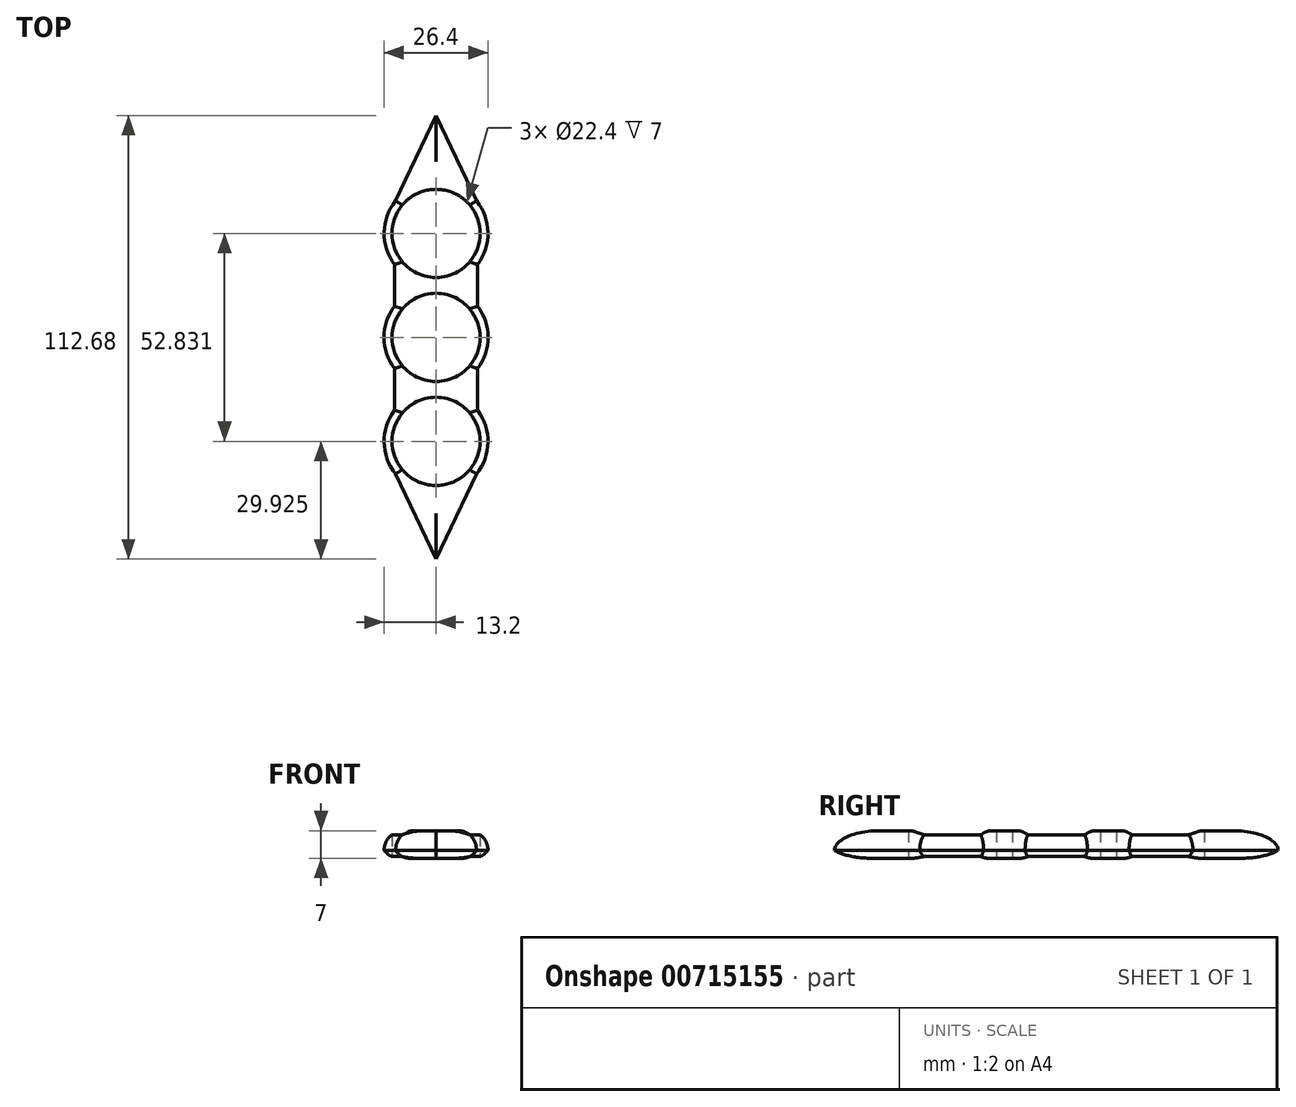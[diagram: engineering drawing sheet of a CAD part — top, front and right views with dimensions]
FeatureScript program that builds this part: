
annotation { "Feature Type Name" : "Feature", "Feature Type Description" : "" }
export const myFeature = defineFeature(function(context is Context, id is Id, definition is map)
    precondition{}
    {
        {
            var Q0;
            Q0=qCreatedBy(makeId("Top.planeOp"),FACE);
            var sketch = newSketch(context, id + "F0", { "sketchPlane" : qUnion([Q0])});
            skCircle(sketch, "E0", {"center": v(0, 0) * mm, "radius": 11.2 * mm});
            skCircle(sketch, "E1", {"center": v(0, 0) * mm, "radius": 13.2 * mm});
            skCircle(sketch, "E2", {"center": v(0, 26.42) * mm, "radius": 11.2 * mm});
            skArc(sketch, "E3", {"start": v(10.55, 18.48) * mm, "mid": v(0, 39.62) * mm, "end": v(-10.55, 18.48) * mm});
            skArc(sketch, "E4.1.0", {"start": v(-10.55, -18.48) * mm, "mid": v(0, -39.62) * mm, "end": v(10.55, -18.48) * mm});
            skCircle(sketch, "E4.1.1", {"center": v(0, -26.42) * mm, "radius": 11.2 * mm});
            skLineSegment(sketch, "E5", {"start": v(-10.55, 18.48) * mm, "end": v(-10.55, 7.93) * mm});
            skLineSegment(sketch, "E6", {"start": v(10.55, 18.48) * mm, "end": v(10.55, 7.93) * mm});
            skLineSegment(sketch, "E7.1.0", {"start": v(-10.55, -18.48) * mm, "end": v(-10.55, -7.93) * mm});
            skLineSegment(sketch, "E7.1.1", {"start": v(10.55, -18.48) * mm, "end": v(10.55, -7.93) * mm});
            skLineSegment(sketch, "E8", {"start": v(10.28, 34.7) * mm, "end": v(0, 56.34) * mm});
            skPoint(sketch, "E8.endSnap0", {"position": v(0, 39.62) * mm});
            skLineSegment(sketch, "E9", {"start": v(0, 56.34) * mm, "end": v(-10.28, 34.7) * mm});
            skLineSegment(sketch, "E10.1.0", {"start": v(0, -56.34) * mm, "end": v(10.28, -34.7) * mm});
            skLineSegment(sketch, "E10.1.1", {"start": v(-10.28, -34.7) * mm, "end": v(0, -56.34) * mm});
            skSolve(sketch);
        }
        {
            var Q0;
            {var subQ0=sQuery(id+"F0.wireOp",EDGE,"E10.1.0");Q0=makeQuery(id+"F0.imprint","IMPRINT",FACE,{"disambiguationData":[TD([[makeQuery(id+"F0.imprint","IMPRINT",EDGE,{"derivedFrom":subQ0}),1.0]])]});}
            var Q1;
            Q1=makeQuery(id+"F0.imprint","IMPRINT",FACE,{"disambiguationData":[TD([[makeQuery(id+"F0.imprint","IMPRINT",EDGE,{"derivedFrom":sQuery(id+"F0.wireOp",EDGE,"E4.1.1")}),-1.0]])]});
            var Q2;
            Q2=makeQuery(id+"F0.imprint","IMPRINT",FACE,{"disambiguationData":[TD([[makeQuery(id+"F0.imprint","IMPRINT",EDGE,{"derivedFrom":sQuery(id+"F0.wireOp",EDGE,"E0")}),-1.0]])]});
            var Q3;
            Q3=makeQuery(id+"F0.imprint","IMPRINT",FACE,{"disambiguationData":[TD([[makeQuery(id+"F0.imprint","IMPRINT",EDGE,{"derivedFrom":sQuery(id+"F0.wireOp",EDGE,"E2")}),-1.0]])]});
            var Q4;
            {var subQ0=sQuery(id+"F0.wireOp",EDGE,"E8");Q4=makeQuery(id+"F0.imprint","IMPRINT",FACE,{"disambiguationData":[TD([[makeQuery(id+"F0.imprint","IMPRINT",EDGE,{"derivedFrom":subQ0}),1.0]])]});}
            extrude(context, id + "F1", {"entities" : qUnion([Q0, Q1, Q2, Q3, Q4]), "depth" : 7 * mm, "offsetDistance" : 25 * mm});
        }
        {
            var Q0;
            Q0=makeQuery(id+"F1.opExtrude","CAP_EDGE",EDGE,{"disambiguationData":[OSD([sQuery(id+"F0.wireOp",EDGE,"E10.1.0")])],"isStart":false});
            var Q1;
            {var subQ0=sQuery(id+"F0.wireOp",EDGE,"E4.1.0");Q1=makeQuery(id+"F1.opExtrude","CAP_EDGE",EDGE,{"disambiguationData":[OSD([subQ0]),TDD([makeQuery(id+"F0.imprint","IMPRINT",EDGE,{"disambiguationData":[TD([[makeQuery(id+"F0.imprint","INTERSECT",VERTEX,{"derivedFrom":[subQ0,sQuery(id+"F0.wireOp",EDGE,"E7.1.1")]}),1.0]])],"derivedFrom":subQ0})])],"isStart":false});}
            var Q2;
            Q2=makeQuery(id+"F1.opExtrude","CAP_EDGE",EDGE,{"disambiguationData":[OSD([sQuery(id+"F0.wireOp",EDGE,"E7.1.1")])],"isStart":false});
            var Q3;
            {var subQ0=sQuery(id+"F0.wireOp",EDGE,"E1");Q3=makeQuery(id+"F1.opExtrude","CAP_EDGE",EDGE,{"disambiguationData":[OSD([subQ0]),TDD([makeQuery(id+"F0.imprint","IMPRINT",EDGE,{"disambiguationData":[TD([[makeQuery(id+"F0.imprint","INTERSECT",VERTEX,{"derivedFrom":[subQ0,sQuery(id+"F0.wireOp",EDGE,"E6")]}),1.0]])],"derivedFrom":subQ0})])],"isStart":false});}
            var Q4;
            Q4=makeQuery(id+"F1.opExtrude","CAP_EDGE",EDGE,{"disambiguationData":[OSD([sQuery(id+"F0.wireOp",EDGE,"E6")])],"isStart":false});
            var Q5;
            {var subQ0=sQuery(id+"F0.wireOp",EDGE,"E3");Q5=makeQuery(id+"F1.opExtrude","CAP_EDGE",EDGE,{"disambiguationData":[OSD([subQ0]),TDD([makeQuery(id+"F0.imprint","IMPRINT",EDGE,{"disambiguationData":[TD([[makeQuery(id+"F0.imprint","INTERSECT",VERTEX,{"derivedFrom":[subQ0,sQuery(id+"F0.wireOp",EDGE,"E6")]}),-1.0]])],"derivedFrom":subQ0})])],"isStart":false});}
            var Q6;
            Q6=makeQuery(id+"F1.opExtrude","CAP_EDGE",EDGE,{"disambiguationData":[OSD([sQuery(id+"F0.wireOp",EDGE,"E8")])],"isStart":false});
            var Q7;
            Q7=makeQuery(id+"F1.opExtrude","CAP_EDGE",EDGE,{"disambiguationData":[OSD([sQuery(id+"F0.wireOp",EDGE,"E9")])],"isStart":false});
            var Q8;
            {var subQ0=sQuery(id+"F0.wireOp",EDGE,"E3");Q8=makeQuery(id+"F1.opExtrude","CAP_EDGE",EDGE,{"disambiguationData":[OSD([subQ0]),TDD([makeQuery(id+"F0.imprint","IMPRINT",EDGE,{"disambiguationData":[TD([[makeQuery(id+"F0.imprint","INTERSECT",VERTEX,{"derivedFrom":[subQ0,sQuery(id+"F0.wireOp",EDGE,"E5")]}),1.0]])],"derivedFrom":subQ0})])],"isStart":false});}
            var Q9;
            Q9=makeQuery(id+"F1.opExtrude","CAP_EDGE",EDGE,{"disambiguationData":[OSD([sQuery(id+"F0.wireOp",EDGE,"E5")])],"isStart":false});
            var Q10;
            {var subQ0=sQuery(id+"F0.wireOp",EDGE,"E1");Q10=makeQuery(id+"F1.opExtrude","CAP_EDGE",EDGE,{"disambiguationData":[OSD([subQ0]),TDD([makeQuery(id+"F0.imprint","IMPRINT",EDGE,{"disambiguationData":[TD([[makeQuery(id+"F0.imprint","INTERSECT",VERTEX,{"derivedFrom":[subQ0,sQuery(id+"F0.wireOp",EDGE,"E5")]}),-1.0]])],"derivedFrom":subQ0})])],"isStart":false});}
            var Q11;
            Q11=makeQuery(id+"F1.opExtrude","CAP_EDGE",EDGE,{"disambiguationData":[OSD([sQuery(id+"F0.wireOp",EDGE,"E7.1.0")])],"isStart":false});
            var Q12;
            {var subQ0=sQuery(id+"F0.wireOp",EDGE,"E4.1.0");Q12=makeQuery(id+"F1.opExtrude","CAP_EDGE",EDGE,{"disambiguationData":[OSD([subQ0]),TDD([makeQuery(id+"F0.imprint","IMPRINT",EDGE,{"disambiguationData":[TD([[makeQuery(id+"F0.imprint","INTERSECT",VERTEX,{"derivedFrom":[subQ0,sQuery(id+"F0.wireOp",EDGE,"E7.1.0")]}),-1.0]])],"derivedFrom":subQ0})])],"isStart":false});}
            var Q13;
            Q13=makeQuery(id+"F1.opExtrude","CAP_EDGE",EDGE,{"disambiguationData":[OSD([sQuery(id+"F0.wireOp",EDGE,"E10.1.1")])],"isStart":false});
            fillet(context, id + "F2", {"entities" : qUnion([Q0, Q1, Q2, Q3, Q4, Q5, Q6, Q7, Q8, Q9, Q10, Q11, Q12, Q13]), "radius" : 5 * mm, "tangentPropagation" : true, "allowEdgeOverflow" : false});
        }
        {
            var Q0;
            Q0=makeQuery(id+"F1.opExtrude","CAP_EDGE",EDGE,{"disambiguationData":[OSD([sQuery(id+"F0.wireOp",EDGE,"E10.1.1")])],"isStart":true});
            var Q1;
            Q1=makeQuery(id+"F1.opExtrude","CAP_EDGE",EDGE,{"disambiguationData":[OSD([sQuery(id+"F0.wireOp",EDGE,"E7.1.0")])],"isStart":true});
            var Q2;
            Q2=makeQuery(id+"F1.opExtrude","CAP_EDGE",EDGE,{"disambiguationData":[OSD([sQuery(id+"F0.wireOp",EDGE,"E5")])],"isStart":true});
            var Q3;
            Q3=makeQuery(id+"F1.opExtrude","CAP_EDGE",EDGE,{"disambiguationData":[OSD([sQuery(id+"F0.wireOp",EDGE,"E6")])],"isStart":true});
            var Q4;
            Q4=makeQuery(id+"F1.opExtrude","CAP_EDGE",EDGE,{"disambiguationData":[OSD([sQuery(id+"F0.wireOp",EDGE,"E7.1.1")])],"isStart":true});
            var Q5;
            Q5=makeQuery(id+"F1.opExtrude","CAP_EDGE",EDGE,{"disambiguationData":[OSD([sQuery(id+"F0.wireOp",EDGE,"E10.1.0")])],"isStart":true});
            var Q6;
            Q6=makeQuery(id+"F1.opExtrude","CAP_EDGE",EDGE,{"disambiguationData":[OSD([sQuery(id+"F0.wireOp",EDGE,"E8")])],"isStart":true});
            var Q7;
            Q7=makeQuery(id+"F1.opExtrude","CAP_EDGE",EDGE,{"disambiguationData":[OSD([sQuery(id+"F0.wireOp",EDGE,"E9")])],"isStart":true});
            fillet(context, id + "F3", {"entities" : qUnion([Q0, Q1, Q2, Q3, Q4, Q5, Q6, Q7]), "radius" : 5 * mm, "tangentPropagation" : true, "allowEdgeOverflow" : false});
        }
        {
            var Q0;
            {var subQ0=sQuery(id+"F0.wireOp",EDGE,"E1");Q0=makeQuery(id+"F1.opExtrude","CAP_EDGE",EDGE,{"disambiguationData":[OSD([subQ0]),TDD([makeQuery(id+"F0.imprint","IMPRINT",EDGE,{"disambiguationData":[TD([[makeQuery(id+"F0.imprint","INTERSECT",VERTEX,{"derivedFrom":[subQ0,sQuery(id+"F0.wireOp",EDGE,"E6")]}),1.0]])],"derivedFrom":subQ0})])],"isStart":true});}
            var Q1;
            {var subQ0=sQuery(id+"F0.wireOp",EDGE,"E1");Q1=makeQuery(id+"F1.opExtrude","CAP_EDGE",EDGE,{"disambiguationData":[OSD([subQ0]),TDD([makeQuery(id+"F0.imprint","IMPRINT",EDGE,{"disambiguationData":[TD([[makeQuery(id+"F0.imprint","INTERSECT",VERTEX,{"derivedFrom":[subQ0,sQuery(id+"F0.wireOp",EDGE,"E5")]}),-1.0]])],"derivedFrom":subQ0})])],"isStart":true});}
            var Q2;
            {var subQ0=sQuery(id+"F0.wireOp",EDGE,"E4.1.0");Q2=makeQuery(id+"F1.opExtrude","CAP_EDGE",EDGE,{"disambiguationData":[OSD([subQ0]),TDD([makeQuery(id+"F0.imprint","IMPRINT",EDGE,{"disambiguationData":[TD([[makeQuery(id+"F0.imprint","INTERSECT",VERTEX,{"derivedFrom":[subQ0,sQuery(id+"F0.wireOp",EDGE,"E7.1.1")]}),1.0]])],"derivedFrom":subQ0})])],"isStart":true});}
            var Q3;
            {var subQ0=sQuery(id+"F0.wireOp",EDGE,"E4.1.0");Q3=makeQuery(id+"F1.opExtrude","CAP_EDGE",EDGE,{"disambiguationData":[OSD([subQ0]),TDD([makeQuery(id+"F0.imprint","IMPRINT",EDGE,{"disambiguationData":[TD([[makeQuery(id+"F0.imprint","INTERSECT",VERTEX,{"derivedFrom":[subQ0,sQuery(id+"F0.wireOp",EDGE,"E7.1.0")]}),-1.0]])],"derivedFrom":subQ0})])],"isStart":true});}
            var Q4;
            {var subQ0=sQuery(id+"F0.wireOp",EDGE,"E3");Q4=makeQuery(id+"F1.opExtrude","CAP_EDGE",EDGE,{"disambiguationData":[OSD([subQ0]),TDD([makeQuery(id+"F0.imprint","IMPRINT",EDGE,{"disambiguationData":[TD([[makeQuery(id+"F0.imprint","INTERSECT",VERTEX,{"derivedFrom":[subQ0,sQuery(id+"F0.wireOp",EDGE,"E6")]}),-1.0]])],"derivedFrom":subQ0})])],"isStart":true});}
            var Q5;
            {var subQ0=sQuery(id+"F0.wireOp",EDGE,"E3");Q5=makeQuery(id+"F1.opExtrude","CAP_EDGE",EDGE,{"disambiguationData":[OSD([subQ0]),TDD([makeQuery(id+"F0.imprint","IMPRINT",EDGE,{"disambiguationData":[TD([[makeQuery(id+"F0.imprint","INTERSECT",VERTEX,{"derivedFrom":[subQ0,sQuery(id+"F0.wireOp",EDGE,"E5")]}),1.0]])],"derivedFrom":subQ0})])],"isStart":true});}
            fillet(context, id + "F4", {"entities" : qUnion([Q0, Q1, Q2, Q3, Q4, Q5]), "radius" : 5 * mm, "tangentPropagation" : true, "allowEdgeOverflow" : false});
        }
    });
